# Revit family: 6705
name_source: partatom
category: Plumbing Fixtures
units: mm (PartAtom-declared; Revit-internal decimal feet)

## family parameters
Cut with Voids When Loaded = No
Host = Face
OmniClass Number = 23.65.70.11.11
OmniClass Title = Fixtures for Liquids
Part Type = Normal
Room Calculation Point = No
Round Connector Dimension = Use Diameter
Shared = No

## types (2) — shared parameters
Date Modified = January 30, 2015
Family Version = 1.0
Gallons Per Minute = 0.000 GPM
Manufacturer = Symmons Industries, Inc.
Model Disclaimer = Contact Symmons Industries, Inc. For More Information
Product Documentation Link = http://www.symmons.com
Product Page URL = http://www.symmons.com
Product data url = https://bimobject.com
URL = http://www.symmons.com
z Error = No
z GPM GPM = 0.000 GPM
z Has Rebuild Kit Trim Only = No
z Has Trim = No
zero-valued in all types: Default Elevation, z GPM Number, z Type GPM

## per-type parameters (varying)
| type | Description | Equipment Abbreviation | Model | Product Material | z Showerhead | z Type | z Type Finish |
| Chrome | Shower System with Symmons Temptrol mixing valve, Chrome | TSS | 3501-CYL-B | Chrome - Symmons - Polished | Showerhead | 1 | 1 |
| Satin Nickel | Shower System with Symmons Temptrol mixing valve, Satin Nickel | SSV | 3501-CYL-B-STN | Nickel - Symmons - Satin |  | 2 | 2 |

## geometry (parser evidence)
native form markers: Blend x2, Sweep x8
no freeform markers — native parametric forms only
